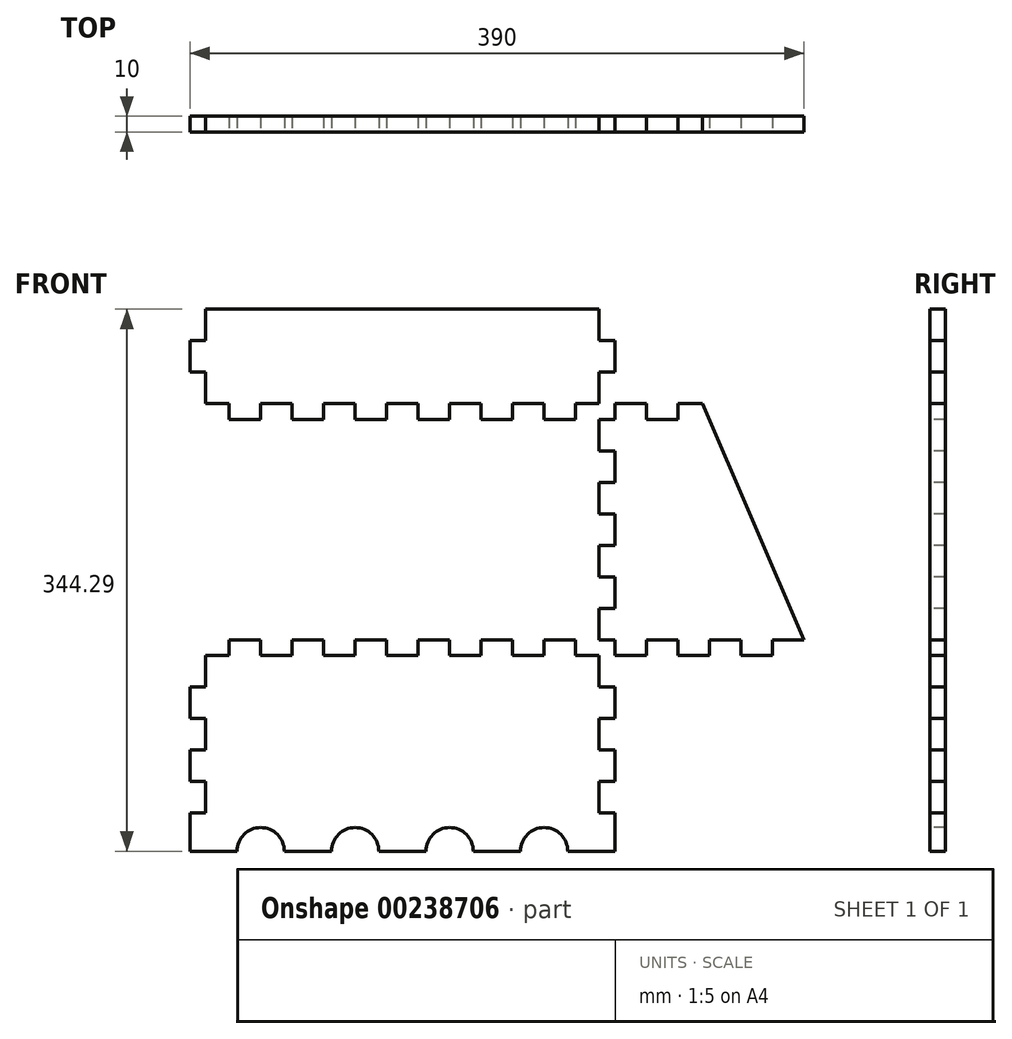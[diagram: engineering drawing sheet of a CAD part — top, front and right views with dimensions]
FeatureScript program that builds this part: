
annotation { "Feature Type Name" : "Feature", "Feature Type Description" : "" }
export const myFeature = defineFeature(function(context is Context, id is Id, definition is map)
    precondition{}
    {
        {
            var Q0;
            Q0=qCreatedBy(makeId("Front.planeOp"),FACE);
            var sketch = newSketch(context, id + "F0", { "sketchPlane" : qUnion([Q0])});
            skLineSegment(sketch, "E0.bottom", {"start": v(0, -100) * mm, "end": v(250, -100) * mm, "construction": true});
            skLineSegment(sketch, "E0.top", {"start": v(0, 40) * mm, "end": v(250, 40) * mm, "construction": true});
            skLineSegment(sketch, "E0.right", {"start": v(250, -100) * mm, "end": v(250, 40) * mm, "construction": true});
            skLineSegment(sketch, "E1", {"start": v(125, -92.5) * mm, "end": v(125, -100) * mm, "construction": true});
            skLineSegment(sketch, "E2.top", {"start": v(135, -110) * mm, "end": v(115, -110) * mm});
            skLineSegment(sketch, "E2.left", {"start": v(135, -100) * mm, "end": v(135, -110) * mm});
            skLineSegment(sketch, "E2.right", {"start": v(115, -100) * mm, "end": v(115, -110) * mm});
            skPoint(sketch, "E2.middle", {"position": v(125, -105) * mm});
            skLineSegment(sketch, "E3", {"start": v(135, -100) * mm, "end": v(155, -100) * mm});
            skLineSegment(sketch, "E4.1.0.0", {"start": v(155, -100) * mm, "end": v(155, -110) * mm});
            skLineSegment(sketch, "E4.1.0.1", {"start": v(175, -110) * mm, "end": v(155, -110) * mm});
            skLineSegment(sketch, "E4.1.0.2", {"start": v(175, -100) * mm, "end": v(175, -110) * mm});
            skLineSegment(sketch, "E4.1.0.3", {"start": v(175, -100) * mm, "end": v(195, -100) * mm});
            skLineSegment(sketch, "E4.2.0.0", {"start": v(195, -100) * mm, "end": v(195, -110) * mm});
            skLineSegment(sketch, "E4.2.0.1", {"start": v(215, -110) * mm, "end": v(195, -110) * mm});
            skLineSegment(sketch, "E4.2.0.2", {"start": v(215, -100) * mm, "end": v(215, -110) * mm});
            skLineSegment(sketch, "E4.2.0.3", {"start": v(215, -100) * mm, "end": v(235, -100) * mm});
            skLineSegment(sketch, "E4.direction1", {"start": v(115, -110) * mm, "end": v(155, -110) * mm, "construction": true});
            skLineSegment(sketch, "E5.0.3.0", {"start": v(235, -100) * mm, "end": v(235, -110) * mm});
            skLineSegment(sketch, "E6.MirrorCS", {"start": v(15, -100) * mm, "end": v(15, -110) * mm});
            skLineSegment(sketch, "E7.MirrorCS", {"start": v(35, -100) * mm, "end": v(35, -110) * mm});
            skLineSegment(sketch, "E8.MirrorCS", {"start": v(35, -110) * mm, "end": v(55, -110) * mm});
            skLineSegment(sketch, "E9.MirrorCS", {"start": v(55, -100) * mm, "end": v(55, -110) * mm});
            skLineSegment(sketch, "E10.MirrorCS", {"start": v(75, -100) * mm, "end": v(75, -110) * mm});
            skLineSegment(sketch, "E11.MirrorCS", {"start": v(75, -110) * mm, "end": v(95, -110) * mm});
            skLineSegment(sketch, "E12.MirrorCS", {"start": v(95, -100) * mm, "end": v(95, -110) * mm});
            skLineSegment(sketch, "E13.MirrorCS", {"start": v(35, -100) * mm, "end": v(15, -100) * mm});
            skLineSegment(sketch, "E14.MirrorCS", {"start": v(115, -100) * mm, "end": v(95, -100) * mm});
            skLineSegment(sketch, "E15.MirrorCS", {"start": v(75, -100) * mm, "end": v(55, -100) * mm});
            skLineSegment(sketch, "E16.bottom", {"start": v(250, -20) * mm, "end": v(260, -20) * mm});
            skLineSegment(sketch, "E16.top", {"start": v(250, -40) * mm, "end": v(260, -40) * mm});
            skLineSegment(sketch, "E16.right", {"start": v(260, -20) * mm, "end": v(260, -40) * mm});
            skPoint(sketch, "E16.middle", {"position": v(255, -30) * mm});
            skPoint(sketch, "E16.middle.positionSnap0", {"position": v(250, -30) * mm});
            skPoint(sketch, "E16.centerSnap0", {"position": v(250, -30) * mm});
            skLineSegment(sketch, "E17", {"start": v(250, -20) * mm, "end": v(250, 0) * mm});
            skLineSegment(sketch, "E18.0.1.0", {"start": v(250, 0) * mm, "end": v(260, 0) * mm});
            skLineSegment(sketch, "E18.0.1.1", {"start": v(260, 20) * mm, "end": v(260, 0) * mm});
            skLineSegment(sketch, "E18.0.1.2", {"start": v(250, 20) * mm, "end": v(260, 20) * mm});
            skLineSegment(sketch, "E18.0.1.3", {"start": v(250, 20) * mm, "end": v(250, 40) * mm});
            skLineSegment(sketch, "E18.0.2.0", {"start": v(250, 40) * mm, "end": v(260, 40) * mm});
            skLineSegment(sketch, "E18.direction1", {"start": v(250, -40) * mm, "end": v(275, -40) * mm, "construction": true});
            skLineSegment(sketch, "E18.direction2", {"start": v(250, -40) * mm, "end": v(250, 0) * mm, "construction": true});
            skLineSegment(sketch, "E19", {"start": v(255, -30) * mm, "end": v(250, -30) * mm, "construction": true});
            skLineSegment(sketch, "E20.MirrorCS", {"start": v(250, -40) * mm, "end": v(250, -60) * mm});
            skLineSegment(sketch, "E21.MirrorCS", {"start": v(250, -60) * mm, "end": v(260, -60) * mm});
            skLineSegment(sketch, "E22.MirrorCS", {"start": v(260, -80) * mm, "end": v(260, -60) * mm});
            skLineSegment(sketch, "E23.MirrorCS", {"start": v(250, -80) * mm, "end": v(260, -80) * mm});
            skLineSegment(sketch, "E24.MirrorCS", {"start": v(250, -80) * mm, "end": v(250, -100) * mm});
            skLineSegment(sketch, "E25.MirrorCS", {"start": v(250, -100) * mm, "end": v(260, -100) * mm});
            skLineSegment(sketch, "E26", {"start": v(235, -110) * mm, "end": v(260, -110) * mm});
            skLineSegment(sketch, "E27", {"start": v(260, -110) * mm, "end": v(260, -100) * mm});
            skLineSegment(sketch, "E28.MirrorCS", {"start": v(35, 40) * mm, "end": v(35, 50) * mm});
            skLineSegment(sketch, "E29.MirrorCS", {"start": v(115, 40) * mm, "end": v(115, 50) * mm});
            skLineSegment(sketch, "E30.MirrorCS", {"start": v(55, 40) * mm, "end": v(55, 50) * mm});
            skLineSegment(sketch, "E31.MirrorCS", {"start": v(155, 40) * mm, "end": v(155, 50) * mm});
            skLineSegment(sketch, "E32.MirrorCS", {"start": v(75, 40) * mm, "end": v(75, 50) * mm});
            skLineSegment(sketch, "E33.MirrorCS", {"start": v(235, 40) * mm, "end": v(235, 50) * mm});
            skLineSegment(sketch, "E34.MirrorCS", {"start": v(95, 40) * mm, "end": v(95, 50) * mm});
            skLineSegment(sketch, "E35.MirrorCS", {"start": v(15, 40) * mm, "end": v(15, 50) * mm});
            skLineSegment(sketch, "E36.MirrorCS", {"start": v(260, 50) * mm, "end": v(260, 40) * mm});
            skLineSegment(sketch, "E37.MirrorCS", {"start": v(175, 40) * mm, "end": v(175, 50) * mm});
            skLineSegment(sketch, "E38.MirrorCS", {"start": v(195, 40) * mm, "end": v(195, 50) * mm});
            skLineSegment(sketch, "E39.MirrorCS", {"start": v(135, 40) * mm, "end": v(135, 50) * mm});
            skLineSegment(sketch, "E40.MirrorCS", {"start": v(215, 40) * mm, "end": v(215, 50) * mm});
            skLineSegment(sketch, "E41.MirrorCS", {"start": v(135, 40) * mm, "end": v(155, 40) * mm});
            skLineSegment(sketch, "E42.MirrorCS", {"start": v(215, 40) * mm, "end": v(235, 40) * mm});
            skLineSegment(sketch, "E43.MirrorCS", {"start": v(175, 40) * mm, "end": v(195, 40) * mm});
            skLineSegment(sketch, "E44.MirrorCS", {"start": v(35, 40) * mm, "end": v(15, 40) * mm});
            skLineSegment(sketch, "E45.MirrorCS", {"start": v(115, 40) * mm, "end": v(95, 40) * mm});
            skLineSegment(sketch, "E46.MirrorCS", {"start": v(75, 40) * mm, "end": v(55, 40) * mm});
            skLineSegment(sketch, "E47.MirrorCS", {"start": v(135, 50) * mm, "end": v(115, 50) * mm});
            skLineSegment(sketch, "E48.MirrorCS", {"start": v(35, 50) * mm, "end": v(55, 50) * mm});
            skLineSegment(sketch, "E49.MirrorCS", {"start": v(175, 50) * mm, "end": v(155, 50) * mm});
            skLineSegment(sketch, "E50.MirrorCS", {"start": v(215, 50) * mm, "end": v(195, 50) * mm});
            skLineSegment(sketch, "E51.MirrorCS", {"start": v(75, 50) * mm, "end": v(95, 50) * mm});
            skLineSegment(sketch, "E52.MirrorCS", {"start": v(235, 50) * mm, "end": v(260, 50) * mm});
            skLineSegment(sketch, "E53.MirrorCS", {"start": v(15, -110) * mm, "end": v(-10, -110) * mm});
            skLineSegment(sketch, "E54.MirrorCS", {"start": v(-10, -110) * mm, "end": v(-10, -100) * mm});
            skLineSegment(sketch, "E55.MirrorCS", {"start": v(0, -100) * mm, "end": v(-10, -100) * mm});
            skLineSegment(sketch, "E56.MirrorCS", {"start": v(0, -80) * mm, "end": v(-10, -80) * mm});
            skLineSegment(sketch, "E57.MirrorCS", {"start": v(-10, -80) * mm, "end": v(-10, -60) * mm});
            skLineSegment(sketch, "E58.MirrorCS", {"start": v(0, -60) * mm, "end": v(-10, -60) * mm});
            skLineSegment(sketch, "E59.MirrorCS", {"start": v(0, -100) * mm, "end": v(0, 40) * mm, "construction": true});
            skLineSegment(sketch, "E60.MirrorCS", {"start": v(-10, -20) * mm, "end": v(-10, -40) * mm, "construction": true});
            skLineSegment(sketch, "E61.MirrorCS", {"start": v(0, -20) * mm, "end": v(-10, -20) * mm});
            skLineSegment(sketch, "E62.MirrorCS", {"start": v(0, 0) * mm, "end": v(-10, 0) * mm});
            skLineSegment(sketch, "E63.MirrorCS", {"start": v(-10, 20) * mm, "end": v(-10, 0) * mm});
            skLineSegment(sketch, "E64.MirrorCS", {"start": v(0, 20) * mm, "end": v(-10, 20) * mm});
            skLineSegment(sketch, "E65.MirrorCS", {"start": v(0, 40) * mm, "end": v(-10, 40) * mm});
            skLineSegment(sketch, "E66.MirrorCS", {"start": v(-10, 50) * mm, "end": v(-10, 40) * mm});
            skLineSegment(sketch, "E67.MirrorCS", {"start": v(0, 20) * mm, "end": v(0, 40) * mm});
            skLineSegment(sketch, "E68.MirrorCS", {"start": v(0, -20) * mm, "end": v(0, 0) * mm});
            skLineSegment(sketch, "E69.MirrorCS", {"start": v(0, -40) * mm, "end": v(0, -60) * mm});
            skLineSegment(sketch, "E70.MirrorCS", {"start": v(0, -80) * mm, "end": v(0, -100) * mm});
            skLineSegment(sketch, "E71.MirrorCS", {"start": v(0, -40) * mm, "end": v(-10, -40) * mm});
            skLineSegment(sketch, "E72", {"start": v(-10, 50) * mm, "end": v(15, 50) * mm});
            skLineSegment(sketch, "E73.left", {"start": v(-10, -110) * mm, "end": v(-10, -234.29) * mm, "construction": true});
            skLineSegment(sketch, "E73.right", {"start": v(260, -110) * mm, "end": v(260, -234.29) * mm, "construction": true});
            skLineSegment(sketch, "E74.bottom", {"start": v(260, 50) * mm, "end": v(-10, 50) * mm, "construction": true});
            skLineSegment(sketch, "E74.top", {"start": v(260, 110) * mm, "end": v(-10, 110) * mm});
            skLineSegment(sketch, "E74.left", {"start": v(260, 50) * mm, "end": v(260, 110) * mm, "construction": true});
            skLineSegment(sketch, "E74.right", {"start": v(-10, 50) * mm, "end": v(-10, 110) * mm, "construction": true});
            skLineSegment(sketch, "E75.bottom", {"start": v(260, 40) * mm, "end": v(320, 40) * mm, "construction": true});
            skLineSegment(sketch, "E75.top", {"start": v(260, -100) * mm, "end": v(380, -100) * mm, "construction": true});
            skLineSegment(sketch, "E75.right", {"start": v(320, 40) * mm, "end": v(380, -100) * mm});
            skLineSegment(sketch, "E76.top", {"start": v(260, -110) * mm, "end": v(280, -110) * mm});
            skLineSegment(sketch, "E76.left", {"start": v(260, -100) * mm, "end": v(260, -110) * mm});
            skLineSegment(sketch, "E76.right", {"start": v(280, -100) * mm, "end": v(280, -110) * mm});
            skLineSegment(sketch, "E77", {"start": v(280, -100) * mm, "end": v(300, -100) * mm});
            skLineSegment(sketch, "E78.1.0.0", {"start": v(320, -100) * mm, "end": v(340, -100) * mm});
            skLineSegment(sketch, "E78.1.0.1", {"start": v(320, -100) * mm, "end": v(320, -110) * mm});
            skLineSegment(sketch, "E78.1.0.2", {"start": v(300, -110) * mm, "end": v(320, -110) * mm});
            skLineSegment(sketch, "E78.1.0.3", {"start": v(300, -100) * mm, "end": v(300, -110) * mm});
            skLineSegment(sketch, "E78.2.0.0", {"start": v(360, -100) * mm, "end": v(380, -100) * mm});
            skLineSegment(sketch, "E78.2.0.1", {"start": v(360, -100) * mm, "end": v(360, -110) * mm});
            skLineSegment(sketch, "E78.2.0.2", {"start": v(340, -110) * mm, "end": v(360, -110) * mm});
            skLineSegment(sketch, "E78.2.0.3", {"start": v(340, -100) * mm, "end": v(340, -110) * mm});
            skLineSegment(sketch, "E78.direction1", {"start": v(260, -110) * mm, "end": v(300, -110) * mm, "construction": true});
            skLineSegment(sketch, "E79.top", {"start": v(250, -110) * mm, "end": v(250, -130) * mm});
            skLineSegment(sketch, "E79.left", {"start": v(260, -110) * mm, "end": v(250, -110) * mm});
            skLineSegment(sketch, "E79.right", {"start": v(260, -130) * mm, "end": v(250, -130) * mm});
            skLineSegment(sketch, "E80", {"start": v(260, -130) * mm, "end": v(260, -150) * mm});
            skLineSegment(sketch, "E81.1.0.0", {"start": v(260, -170) * mm, "end": v(260, -190) * mm});
            skLineSegment(sketch, "E81.1.0.1", {"start": v(260, -170) * mm, "end": v(250, -170) * mm});
            skLineSegment(sketch, "E81.1.0.2", {"start": v(250, -150) * mm, "end": v(250, -170) * mm});
            skLineSegment(sketch, "E81.1.0.3", {"start": v(260, -150) * mm, "end": v(250, -150) * mm});
            skLineSegment(sketch, "E81.2.0.1", {"start": v(260, -210) * mm, "end": v(250, -210) * mm});
            skLineSegment(sketch, "E81.2.0.2", {"start": v(250, -190) * mm, "end": v(250, -210) * mm});
            skLineSegment(sketch, "E81.2.0.3", {"start": v(260, -190) * mm, "end": v(250, -190) * mm});
            skLineSegment(sketch, "E81.direction1", {"start": v(250, -110) * mm, "end": v(250, -150) * mm, "construction": true});
            skLineSegment(sketch, "E82.MirrorCS", {"start": v(280, 40) * mm, "end": v(280, 50) * mm});
            skLineSegment(sketch, "E83.MirrorCS", {"start": v(280, 40) * mm, "end": v(300, 40) * mm});
            skLineSegment(sketch, "E84.MirrorCS", {"start": v(300, 40) * mm, "end": v(300, 50) * mm});
            skLineSegment(sketch, "E85.MirrorCS", {"start": v(300, 50) * mm, "end": v(320, 50) * mm});
            skLineSegment(sketch, "E86.MirrorCS", {"start": v(320, 40) * mm, "end": v(320, 50) * mm, "construction": true});
            skLineSegment(sketch, "E87.MirrorCS", {"start": v(260, 40) * mm, "end": v(260, 50) * mm});
            skLineSegment(sketch, "E88.MirrorCS", {"start": v(260, 50) * mm, "end": v(280, 50) * mm});
            skLineSegment(sketch, "E89.MirrorCS", {"start": v(250, 50) * mm, "end": v(250, 70) * mm});
            skLineSegment(sketch, "E90.MirrorCS", {"start": v(260, 70) * mm, "end": v(250, 70) * mm});
            skLineSegment(sketch, "E91.MirrorCS", {"start": v(260, 70) * mm, "end": v(260, 90) * mm});
            skLineSegment(sketch, "E92.MirrorCS", {"start": v(260, 90) * mm, "end": v(250, 90) * mm});
            skLineSegment(sketch, "E93.MirrorCS", {"start": v(250, 90) * mm, "end": v(250, 110) * mm});
            skLineSegment(sketch, "E94.MirrorCS", {"start": v(-10, -210) * mm, "end": v(-10, -234.29) * mm});
            skLineSegment(sketch, "E95.MirrorCS", {"start": v(-10, -210) * mm, "end": v(0, -210) * mm});
            skLineSegment(sketch, "E96.MirrorCS", {"start": v(0, -190) * mm, "end": v(0, -210) * mm});
            skLineSegment(sketch, "E97.MirrorCS", {"start": v(-10, -190) * mm, "end": v(0, -190) * mm});
            skLineSegment(sketch, "E98.MirrorCS", {"start": v(-10, -170) * mm, "end": v(-10, -190) * mm});
            skLineSegment(sketch, "E99.MirrorCS", {"start": v(-10, -170) * mm, "end": v(0, -170) * mm});
            skLineSegment(sketch, "E100.MirrorCS", {"start": v(0, -150) * mm, "end": v(0, -170) * mm});
            skLineSegment(sketch, "E101.MirrorCS", {"start": v(-10, -150) * mm, "end": v(0, -150) * mm});
            skLineSegment(sketch, "E102.MirrorCS", {"start": v(-10, -130) * mm, "end": v(-10, -150) * mm});
            skLineSegment(sketch, "E103.MirrorCS", {"start": v(-10, -130) * mm, "end": v(0, -130) * mm});
            skLineSegment(sketch, "E104.MirrorCS", {"start": v(0, -110) * mm, "end": v(0, -150) * mm, "construction": true});
            skLineSegment(sketch, "E105.MirrorCS", {"start": v(0, -110) * mm, "end": v(0, -130) * mm});
            skLineSegment(sketch, "E106.MirrorCS", {"start": v(0, 50) * mm, "end": v(0, 70) * mm});
            skLineSegment(sketch, "E107.MirrorCS", {"start": v(-10, 70) * mm, "end": v(0, 70) * mm});
            skLineSegment(sketch, "E108.MirrorCS", {"start": v(-10, 70) * mm, "end": v(-10, 90) * mm});
            skLineSegment(sketch, "E109.MirrorCS", {"start": v(-10, 90) * mm, "end": v(0, 90) * mm});
            skLineSegment(sketch, "E110.MirrorCS", {"start": v(0, 90) * mm, "end": v(0, 110) * mm});
            skLineSegment(sketch, "E111", {"start": v(320, 40) * mm, "end": v(315.71, 50) * mm});
            skLineSegment(sketch, "E112", {"start": v(380, -100) * mm, "end": v(384.29, -110) * mm, "construction": true});
            skLineSegment(sketch, "E113", {"start": v(384.29, -110) * mm, "end": v(360, -110) * mm, "construction": true});
            skLineSegment(sketch, "E114", {"start": v(260, -210) * mm, "end": v(260, -234.29) * mm});
            skArc(sketch, "E115", {"start": v(19.97, -234.29) * mm, "mid": v(34.99, -219.27) * mm, "end": v(50, -234.29) * mm});
            skLineSegment(sketch, "E116", {"start": v(19.97, -234.29) * mm, "end": v(-10, -234.29) * mm});
            skArc(sketch, "E117.1.0.0", {"start": v(79.98, -234.29) * mm, "mid": v(95, -219.27) * mm, "end": v(110.01, -234.29) * mm});
            skLineSegment(sketch, "E117.1.0.1", {"start": v(79.98, -234.29) * mm, "end": v(50, -234.29) * mm});
            skArc(sketch, "E117.2.0.0", {"start": v(139.99, -234.29) * mm, "mid": v(155, -219.27) * mm, "end": v(170.02, -234.29) * mm});
            skLineSegment(sketch, "E117.2.0.1", {"start": v(139.99, -234.29) * mm, "end": v(110.01, -234.29) * mm});
            skArc(sketch, "E117.3.0.0", {"start": v(200, -234.29) * mm, "mid": v(215.01, -219.27) * mm, "end": v(230.03, -234.29) * mm});
            skLineSegment(sketch, "E117.3.0.1", {"start": v(200, -234.29) * mm, "end": v(170.02, -234.29) * mm});
            skLineSegment(sketch, "E117.4.0.1", {"start": v(260, -234.29) * mm, "end": v(230.03, -234.29) * mm});
            skLineSegment(sketch, "E117.direction1", {"start": v(-10, -234.29) * mm, "end": v(50, -234.29) * mm, "construction": true});
            skSolve(sketch);
        }
        {
            var Q0;
            Q0=makeQuery(id+"F0.imprint","IMPRINT",FACE,{"disambiguationData":[TD([[makeQuery(id+"F0.imprint","IMPRINT",EDGE,{"derivedFrom":sQuery(id+"F0.wireOp",EDGE,"6DD6EAd9-EjR4-M54x-3Gs5-ZzkpjLEBHBt8.bottom")}),1.0]])]});
            var Q1;
            Q1=makeQuery(id+"F0.imprint","IMPRINT",FACE,{"disambiguationData":[TD([[makeQuery(id+"F0.imprint","IMPRINT",EDGE,{"derivedFrom":sQuery(id+"F0.wireOp",EDGE,"3aa721ca-eb7f-4933-b860-b67e4f9833b7.bottom")}),1.0]])]});
            var Q2;
            Q2=makeQuery(id+"F0.imprint","IMPRINT",FACE,{"disambiguationData":[TD([[makeQuery(id+"F0.imprint","IMPRINT",EDGE,{"derivedFrom":sQuery(id+"F0.wireOp",EDGE,"1f1aca45-ddc4-4c07-b0ce-2f99aba2689f.bottom")}),1.0]])]});
            var Q3;
            Q3=makeQuery(id+"F0.imprint","IMPRINT",FACE,{"disambiguationData":[TD([[makeQuery(id+"F0.imprint","IMPRINT",EDGE,{"derivedFrom":sQuery(id+"F0.wireOp",EDGE,"cb640f68-ba69-4848-84fb-c352f3b5514c.1.0.0")}),-1.0]])]});
            var Q4;
            Q4=makeQuery(id+"F0.imprint","IMPRINT",FACE,{"disambiguationData":[TD([[makeQuery(id+"F0.imprint","IMPRINT",EDGE,{"derivedFrom":sQuery(id+"F0.wireOp",EDGE,"be0e698b-39bb-4470-8cd3-9eb53d7fa9ec.3.0.4")}),-1.0]])]});
            var Q5;
            Q5=makeQuery(id+"F0.imprint","IMPRINT",FACE,{"disambiguationData":[TD([[makeQuery(id+"F0.imprint","IMPRINT",EDGE,{"derivedFrom":sQuery(id+"F0.wireOp",EDGE,"be0e698b-39bb-4470-8cd3-9eb53d7fa9ec.2.0.4")}),-1.0]])]});
            var Q6;
            Q6=makeQuery(id+"F0.imprint","IMPRINT",FACE,{"disambiguationData":[TD([[makeQuery(id+"F0.imprint","IMPRINT",EDGE,{"derivedFrom":sQuery(id+"F0.wireOp",EDGE,"be0e698b-39bb-4470-8cd3-9eb53d7fa9ec.1.0.4")}),-1.0]])]});
            var Q7;
            Q7=makeQuery(id+"F0.imprint","IMPRINT",FACE,{"disambiguationData":[TD([[makeQuery(id+"F0.imprint","IMPRINT",EDGE,{"derivedFrom":sQuery(id+"F0.wireOp",EDGE,"KLXXNCfZ-N2lI-LQPs-WN5Q-R0OJi47yWmJK")}),-1.0]])]});
            var Q8;
            Q8=makeQuery(id+"F0.imprint","IMPRINT",FACE,{"disambiguationData":[TD([[makeQuery(id+"F0.imprint","IMPRINT",EDGE,{"derivedFrom":sQuery(id+"F0.wireOp",EDGE,"E2.top")}),1.0]])]});
            var Q9;
            Q9=makeQuery(id+"F0.imprint","IMPRINT",FACE,{"disambiguationData":[TD([[makeQuery(id+"F0.imprint","IMPRINT",EDGE,{"derivedFrom":sQuery(id+"F0.wireOp",EDGE,"E16.bottom")}),1.0]])]});
            var Q10;
            Q10=makeQuery(id+"F0.imprint","IMPRINT",FACE,{"disambiguationData":[TD([[makeQuery(id+"F0.imprint","IMPRINT",EDGE,{"derivedFrom":sQuery(id+"F0.wireOp",EDGE,"E28.MirrorCS")}),1.0]])]});
            extrude(context, id + "F1", {"entities" : qUnion([Q0, Q1, Q2, Q3, Q4, Q5, Q6, Q7, Q8, Q9, Q10]), "oppositeDirection" : true, "depth" : 10 * mm});
        }
    });
